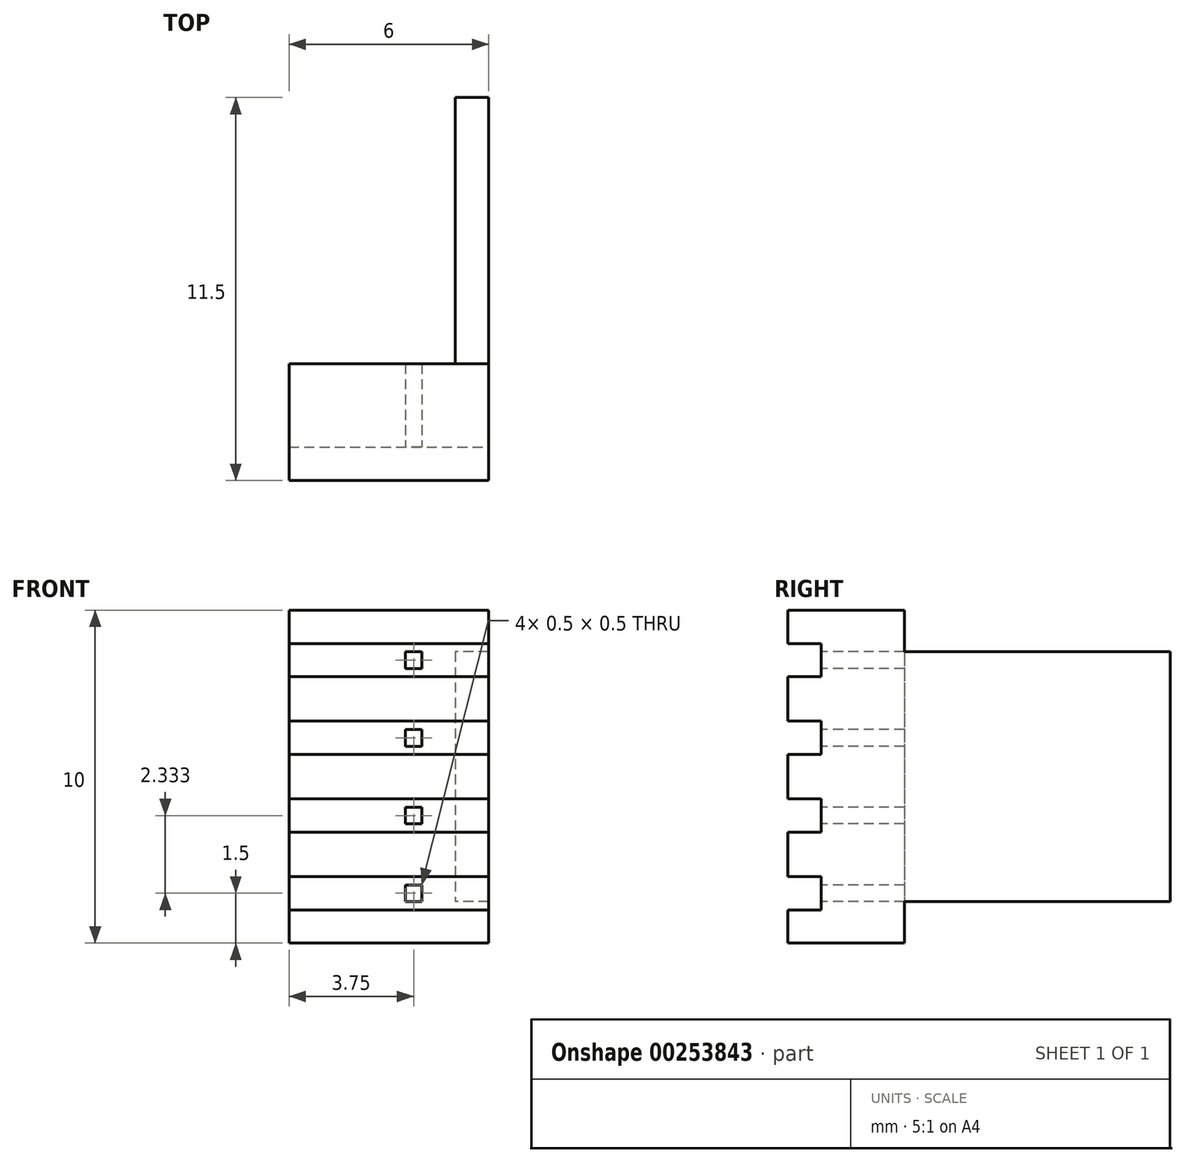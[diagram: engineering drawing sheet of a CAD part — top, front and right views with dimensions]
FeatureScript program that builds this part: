
annotation { "Feature Type Name" : "Feature", "Feature Type Description" : "" }
export const myFeature = defineFeature(function(context is Context, id is Id, definition is map)
    precondition{}
    {
        {
            var Q0;
            Q0=qCreatedBy(makeId("Top.planeOp"),FACE);
            var sketch = newSketch(context, id + "F0", { "sketchPlane" : qUnion([Q0])});
            skLineSegment(sketch, "E0.bottom", {"start": v(0, 0) * mm, "end": v(6, 0) * mm});
            skLineSegment(sketch, "E0.top", {"start": v(5, 11.5) * mm, "end": v(6, 11.5) * mm});
            skLineSegment(sketch, "E0.left", {"start": v(0, 0) * mm, "end": v(0, 3.5) * mm});
            skLineSegment(sketch, "E0.right", {"start": v(6, 0) * mm, "end": v(6, 11.5) * mm});
            skLineSegment(sketch, "E1", {"start": v(5, 11.5) * mm, "end": v(5, 3.5) * mm});
            skLineSegment(sketch, "E2", {"start": v(5, 3.5) * mm, "end": v(0, 3.5) * mm});
            skSolve(sketch);
        }
        {
            var Q0;
            Q0 = qSketchRegion(id + "F0", true);
            extrude(context, id + "F1", {"entities" : qUnion([Q0]), "depth" : 10 * mm});
        }
        {
            var Q0;
            Q0=makeQuery(id+"F1.opExtrude","SWEPT_FACE",FACE,{"disambiguationData":[OSD([sQuery(id+"F0.wireOp",EDGE,"E1")])]});
            var sketch = newSketch(context, id + "F2", { "sketchPlane" : qUnion([Q0])});
            skLineSegment(sketch, "E3.bottom", {"start": v(-11.5, 0) * mm, "end": v(-3.5, 0) * mm});
            skLineSegment(sketch, "E3.top", {"start": v(-11.5, 1.25) * mm, "end": v(-3.5, 1.25) * mm});
            skLineSegment(sketch, "E3.left", {"start": v(-11.5, 0) * mm, "end": v(-11.5, 1.25) * mm});
            skLineSegment(sketch, "E3.right", {"start": v(-3.5, 0) * mm, "end": v(-3.5, 1.25) * mm});
            skLineSegment(sketch, "E4.bottom", {"start": v(-11.5, 10) * mm, "end": v(-3.5, 10) * mm});
            skLineSegment(sketch, "E4.top", {"start": v(-11.5, 8.75) * mm, "end": v(-3.5, 8.75) * mm});
            skLineSegment(sketch, "E4.left", {"start": v(-11.5, 10) * mm, "end": v(-11.5, 8.75) * mm});
            skLineSegment(sketch, "E4.right", {"start": v(-3.5, 10) * mm, "end": v(-3.5, 8.75) * mm});
            skSolve(sketch);
        }
        {
            var Q0;
            Q0 = qSketchRegion(id + "F2", true);
            extrude(context, id + "F3", {"entities" : qUnion([Q0]), "operationType" : NewBodyOperationType.REMOVE, "oppositeDirection" : true, "depth" : 25 * mm});
        }
        {
            var Q0;
            Q0=makeQuery(id+"F1.opExtrude","SWEPT_FACE",FACE,{"disambiguationData":[OSD([sQuery(id+"F0.wireOp",EDGE,"E0.bottom")])]});
            var sketch = newSketch(context, id + "F4", { "sketchPlane" : qUnion([Q0])});
            skLineSegment(sketch, "E5.bottom", {"start": v(3.5, 8.75) * mm, "end": v(4, 8.75) * mm});
            skLineSegment(sketch, "E5.top", {"start": v(3.5, 1.25) * mm, "end": v(4, 1.25) * mm});
            skLineSegment(sketch, "E5.left", {"start": v(3.5, 8.75) * mm, "end": v(3.5, 8.25) * mm});
            skLineSegment(sketch, "E5.right", {"start": v(4, 8.75) * mm, "end": v(4, 8.25) * mm});
            skLineSegment(sketch, "E6", {"start": v(3.5, 8.25) * mm, "end": v(4, 8.25) * mm});
            skLineSegment(sketch, "E7", {"start": v(3.5, 6.42) * mm, "end": v(4, 6.42) * mm});
            skLineSegment(sketch, "E8", {"start": v(3.5, 5.92) * mm, "end": v(4, 5.92) * mm});
            skLineSegment(sketch, "E9", {"start": v(3.5, 4.08) * mm, "end": v(4, 4.08) * mm});
            skLineSegment(sketch, "E10", {"start": v(3.5, 3.58) * mm, "end": v(4, 3.58) * mm});
            skLineSegment(sketch, "E11", {"start": v(3.5, 1.75) * mm, "end": v(4, 1.75) * mm});
            skLineSegment(sketch, "E12.trimOffspring", {"start": v(3.5, 1.75) * mm, "end": v(3.5, 1.25) * mm});
            skLineSegment(sketch, "E13.trimOffspring", {"start": v(4, 1.75) * mm, "end": v(4, 1.25) * mm});
            skLineSegment(sketch, "E14.trimOffspring", {"start": v(3.5, 4.08) * mm, "end": v(3.5, 3.58) * mm});
            skLineSegment(sketch, "E15.trimOffspring", {"start": v(4, 4.08) * mm, "end": v(4, 3.58) * mm});
            skLineSegment(sketch, "E16.trimOffspring", {"start": v(3.5, 6.42) * mm, "end": v(3.5, 5.92) * mm});
            skLineSegment(sketch, "E17.trimOffspring", {"start": v(4, 6.42) * mm, "end": v(4, 5.92) * mm});
            skSolve(sketch);
        }
        {
            var Q0;
            Q0 = qSketchRegion(id + "F4", true);
            extrude(context, id + "F5", {"entities" : qUnion([Q0]), "operationType" : NewBodyOperationType.REMOVE, "oppositeDirection" : true, "depth" : 25 * mm});
        }
        {
            var Q0;
            Q0=makeQuery(id+"F1.opExtrude","SWEPT_FACE",FACE,{"disambiguationData":[OSD([sQuery(id+"F0.wireOp",EDGE,"E0.bottom")])]});
            var sketch = newSketch(context, id + "F6", { "sketchPlane" : qUnion([Q0])});
            skLineSegment(sketch, "E18.bottom", {"start": v(0, 9) * mm, "end": v(6, 9) * mm});
            skLineSegment(sketch, "E18.top", {"start": v(0, 8) * mm, "end": v(6, 8) * mm});
            skLineSegment(sketch, "E18.left", {"start": v(0, 9) * mm, "end": v(0, 8) * mm});
            skLineSegment(sketch, "E18.right", {"start": v(6, 9) * mm, "end": v(6, 8) * mm});
            skLineSegment(sketch, "E19.bottom", {"start": v(0, 6.67) * mm, "end": v(6, 6.67) * mm});
            skLineSegment(sketch, "E19.top", {"start": v(0, 5.67) * mm, "end": v(6, 5.67) * mm});
            skLineSegment(sketch, "E19.left", {"start": v(0, 6.67) * mm, "end": v(0, 5.67) * mm});
            skLineSegment(sketch, "E19.right", {"start": v(6, 6.67) * mm, "end": v(6, 5.67) * mm});
            skLineSegment(sketch, "E20.bottom", {"start": v(0, 4.33) * mm, "end": v(6, 4.33) * mm});
            skLineSegment(sketch, "E20.top", {"start": v(0, 3.33) * mm, "end": v(6, 3.33) * mm});
            skLineSegment(sketch, "E20.left", {"start": v(0, 4.33) * mm, "end": v(0, 3.33) * mm});
            skLineSegment(sketch, "E20.right", {"start": v(6, 4.33) * mm, "end": v(6, 3.33) * mm});
            skLineSegment(sketch, "E21.bottom", {"start": v(0, 2) * mm, "end": v(6, 2) * mm});
            skLineSegment(sketch, "E21.top", {"start": v(0, 1) * mm, "end": v(6, 1) * mm});
            skLineSegment(sketch, "E21.left", {"start": v(0, 2) * mm, "end": v(0, 1) * mm});
            skLineSegment(sketch, "E21.right", {"start": v(6, 2) * mm, "end": v(6, 1) * mm});
            skSolve(sketch);
        }
        {
            var Q0;
            Q0 = qSketchRegion(id + "F6", true);
            extrude(context, id + "F7", {"entities" : qUnion([Q0]), "operationType" : NewBodyOperationType.REMOVE, "oppositeDirection" : true, "depth" : 1 * mm});
        }
    });
